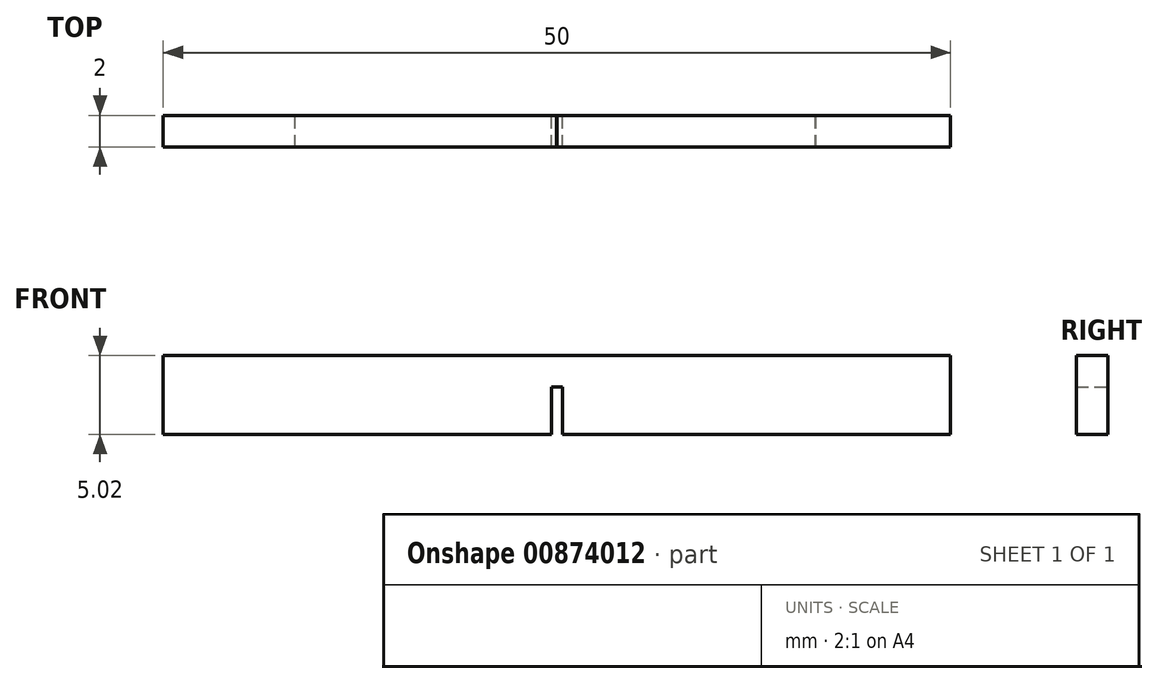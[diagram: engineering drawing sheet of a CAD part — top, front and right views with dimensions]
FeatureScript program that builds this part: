
annotation { "Feature Type Name" : "Feature", "Feature Type Description" : "" }
export const myFeature = defineFeature(function(context is Context, id is Id, definition is map)
    precondition{}
    {
        {
            var Q0;
            Q0=qCreatedBy(makeId("Front.planeOp"),FACE);
            var sketch = newSketch(context, id + "F0", { "sketchPlane" : qUnion([Q0])});
            skLineSegment(sketch, "E0.bottom", {"start": v(0.35, 0) * mm, "end": v(25, 0) * mm});
            skLineSegment(sketch, "E0.top", {"start": v(0, 5) * mm, "end": v(25, 5) * mm});
            skLineSegment(sketch, "E0.right", {"start": v(25, 0) * mm, "end": v(25, 5) * mm});
            skLineSegment(sketch, "E1.top", {"start": v(0, 3) * mm, "end": v(0.35, 3) * mm});
            skLineSegment(sketch, "E1.right", {"start": v(0.35, 0) * mm, "end": v(0.35, 3) * mm});
            skLineSegment(sketch, "E2.MirrorCS", {"start": v(0, 5) * mm, "end": v(-25, 5) * mm});
            skLineSegment(sketch, "E3.MirrorCS", {"start": v(0, 3) * mm, "end": v(-0.35, 3) * mm});
            skLineSegment(sketch, "E4.MirrorCS", {"start": v(-0.35, 0) * mm, "end": v(-0.35, 3) * mm});
            skLineSegment(sketch, "E5.MirrorCS", {"start": v(-0.35, 0) * mm, "end": v(-25, 0) * mm});
            skLineSegment(sketch, "E6.MirrorCS", {"start": v(-25, 0) * mm, "end": v(-25, 5) * mm});
            skSolve(sketch);
        }
        {
            var Q0;
            Q0 = qSketchRegion(id + "F0", true);
            extrude(context, id + "F1", {"entities" : qUnion([Q0]), "depth" : 2 * mm, "offsetDistance" : 25 * mm});
        }
        {
            var Q0;
            Q0=makeQuery(id+"F1.opExtrude","SWEPT_FACE",FACE,{"disambiguationData":[OSD([sQuery(id+"F0.wireOp",EDGE,"E5.MirrorCS")])]});
            var sketch = newSketch(context, id + "F2", { "sketchPlane" : qUnion([Q0])});
            skLineSegment(sketch, "E7.bottom", {"start": v(-16.62, 2) * mm, "end": v(-16.63, 2) * mm});
            skLineSegment(sketch, "E7.top", {"start": v(-16.62, 0) * mm, "end": v(-16.63, 0) * mm});
            skLineSegment(sketch, "E7.left", {"start": v(-16.62, 2) * mm, "end": v(-16.62, 0) * mm});
            skLineSegment(sketch, "E7.right", {"start": v(-16.63, 2) * mm, "end": v(-16.63, 0) * mm});
            skPoint(sketch, "E7.middle", {"position": v(-16.63, 1) * mm});
            skLineSegment(sketch, "E8.bottom", {"start": v(16.45, 2) * mm, "end": v(16.44, 2) * mm});
            skLineSegment(sketch, "E8.top", {"start": v(16.45, 0) * mm, "end": v(16.44, 0) * mm});
            skLineSegment(sketch, "E8.left", {"start": v(16.45, 2) * mm, "end": v(16.45, 0) * mm});
            skLineSegment(sketch, "E8.right", {"start": v(16.44, 2) * mm, "end": v(16.44, 0) * mm});
            skPoint(sketch, "E8.middle", {"position": v(16.45, 1) * mm});
            skSolve(sketch);
        }
        {
            var Q0;
            Q0=makeQuery(id+"F2.imprint","IMPRINT",FACE,{"disambiguationData":[TD([[makeQuery(id+"F2.imprint","IMPRINT",EDGE,{"derivedFrom":sQuery(id+"F2.wireOp",EDGE,"E8.bottom")}),1.0]])]});
            var Q1;
            Q1=makeQuery(id+"F2.imprint","IMPRINT",FACE,{"disambiguationData":[TD([[makeQuery(id+"F2.imprint","IMPRINT",EDGE,{"derivedFrom":sQuery(id+"F2.wireOp",EDGE,"E7.bottom")}),1.0]])]});
            extrude(context, id + "F3", {"entities" : qUnion([Q0, Q1]), "operationType" : NewBodyOperationType.ADD, "depth" : 0.01 * mm, "offsetDistance" : 25 * mm});
        }
        {
            var Q0;
            Q0=makeQuery(id+"F1.opExtrude","SWEPT_FACE",FACE,{"disambiguationData":[OSD([sQuery(id+"F0.wireOp",EDGE,"E0.top"),sQuery(id+"F0.wireOp",EDGE,"E2.MirrorCS")])]});
            var sketch = newSketch(context, id + "F4", { "sketchPlane" : qUnion([Q0])});
            skLineSegment(sketch, "E9.bottom", {"start": v(0, 0) * mm, "end": v(0, 0) * mm});
            skLineSegment(sketch, "E9.top", {"start": v(0, -2) * mm, "end": v(0, -2) * mm});
            skLineSegment(sketch, "E9.left", {"start": v(0, 0) * mm, "end": v(0, -2) * mm});
            skLineSegment(sketch, "E9.right", {"start": v(0, 0) * mm, "end": v(0, -2) * mm});
            skPoint(sketch, "E9.middle", {"position": v(0, -1) * mm});
            skSolve(sketch);
        }
        {
            var Q0;
            Q0=makeQuery(id+"F4.imprint","IMPRINT",FACE,{"disambiguationData":[TD([[makeQuery(id+"F4.imprint","IMPRINT",EDGE,{"derivedFrom":sQuery(id+"F4.wireOp",EDGE,"E9.bottom")}),-1.0]])]});
            extrude(context, id + "F5", {"entities" : qUnion([Q0]), "operationType" : NewBodyOperationType.ADD, "depth" : 0.01 * mm, "offsetDistance" : 25 * mm});
        }
    });
